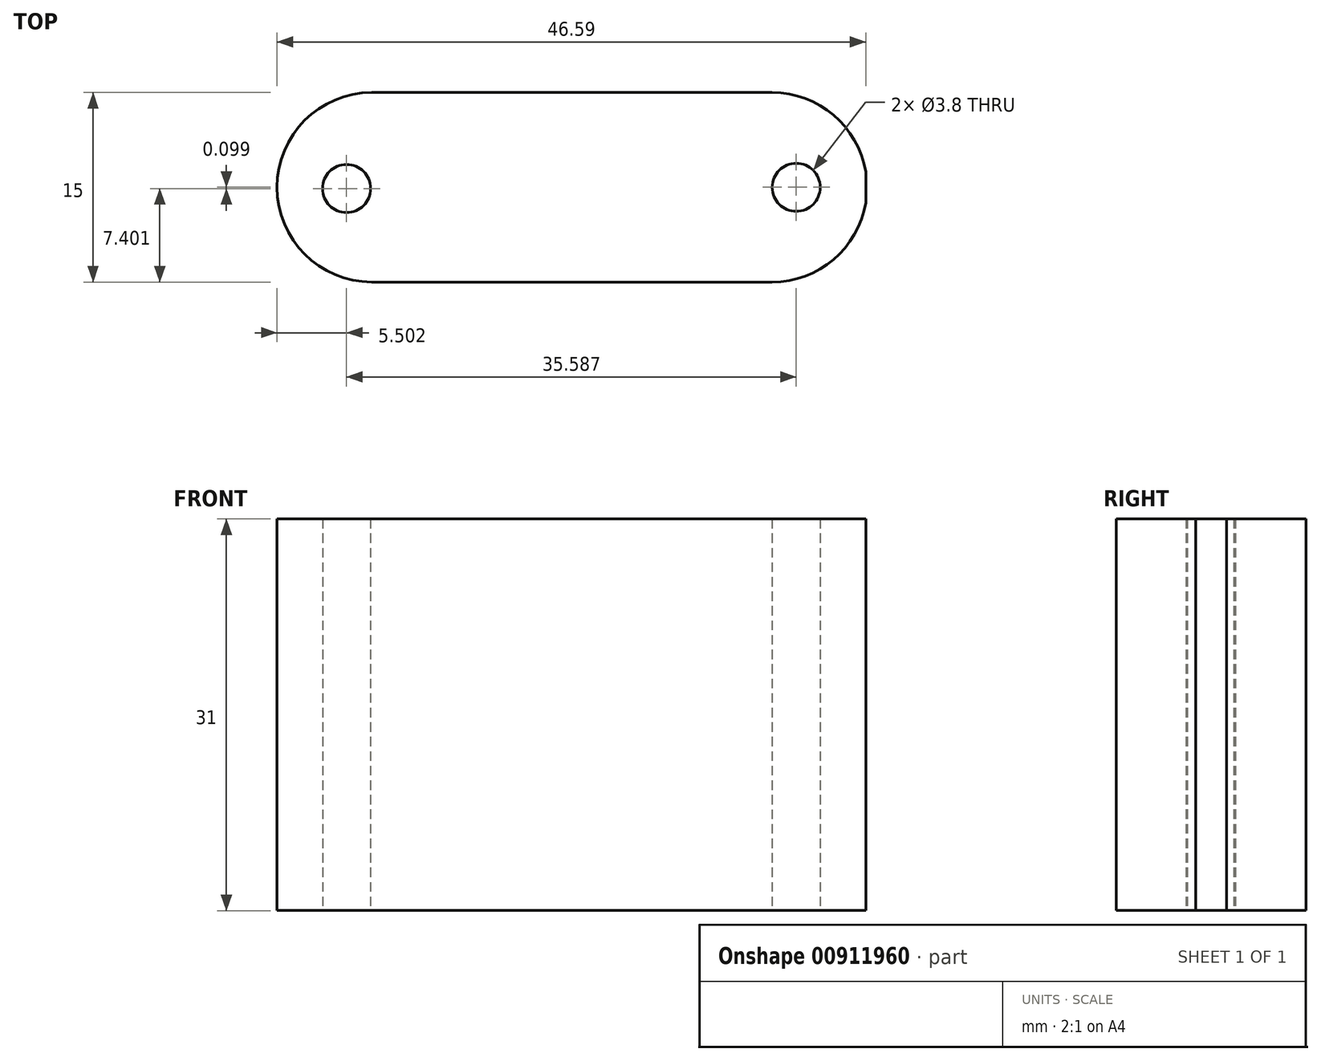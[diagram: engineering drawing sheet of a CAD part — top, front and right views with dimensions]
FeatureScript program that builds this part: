
annotation { "Feature Type Name" : "Feature", "Feature Type Description" : "" }
export const myFeature = defineFeature(function(context is Context, id is Id, definition is map)
    precondition{}
    {
        {
            var Q0;
            Q0=qCreatedBy(makeId("Front.planeOp"),FACE);
            var sketch = newSketch(context, id + "F0", { "sketchPlane" : qUnion([Q0])});
            skLineSegment(sketch, "E0.bottom", {"start": v(-92.62, 11.8) * mm, "end": v(-45.62, 11.8) * mm});
            skLineSegment(sketch, "E0.top", {"start": v(-92.62, -19.2) * mm, "end": v(-45.62, -19.2) * mm});
            skLineSegment(sketch, "E0.left", {"start": v(-92.62, 11.8) * mm, "end": v(-92.62, -19.2) * mm});
            skLineSegment(sketch, "E0.right", {"start": v(-45.62, 11.8) * mm, "end": v(-45.62, -19.2) * mm});
            skSolve(sketch);
        }
        {
            var Q0;
            Q0=qSketchRegion(id+"F0",true);
            extrude(context, id + "F1", {"entities" : qUnion([Q0]), "depth" : 15 * mm, "offsetDistance" : 25 * mm});
        }
        {
            var Q0;
            Q0=makeQuery(id+"F1.opExtrude","SWEPT_FACE",FACE,{"disambiguationData":[OSD([sQuery(id+"F0.wireOp",EDGE,"E0.top")])]});
            var sketch = newSketch(context, id + "F2", { "sketchPlane" : qUnion([Q0])});
            skCircle(sketch, "E1", {"center": v(-51.12, 7.5) * mm, "radius": 1.9 * mm});
            skSolve(sketch);
        }
        {
            var Q0;
            Q0=qSketchRegion(id+"F2",true);
            extrude(context, id + "F3", {"entities" : qUnion([Q0]), "operationType" : NewBodyOperationType.REMOVE, "oppositeDirection" : true, "depth" : 60 * mm, "offsetDistance" : 25 * mm});
        }
        {
            var Q0;
            Q0=makeQuery(id+"F1.opExtrude","SWEPT_FACE",FACE,{"disambiguationData":[OSD([sQuery(id+"F0.wireOp",EDGE,"E0.top")])]});
            var sketch = newSketch(context, id + "F4", { "sketchPlane" : qUnion([Q0])});
            skArc(sketch, "E2", {"start": v(-84.7, 15) * mm, "mid": v(-92.2, 7.5) * mm, "end": v(-84.7, 0) * mm});
            skLineSegment(sketch, "E3", {"start": v(-84.7, 0) * mm, "end": v(-92.62, 0) * mm});
            skLineSegment(sketch, "E4", {"start": v(-92.62, 0) * mm, "end": v(-92.62, 15) * mm});
            skLineSegment(sketch, "E5", {"start": v(-92.62, 15) * mm, "end": v(-84.7, 15) * mm});
            skSolve(sketch);
        }
        {
            var Q0;
            Q0=qSketchRegion(id+"F4",true);
            extrude(context, id + "F5", {"entities" : qUnion([Q0]), "operationType" : NewBodyOperationType.REMOVE, "oppositeDirection" : true, "depth" : 70 * mm, "offsetDistance" : 25 * mm});
        }
        {
            var Q0;
            Q0=makeQuery(id+"F1.opExtrude","SWEPT_FACE",FACE,{"disambiguationData":[OSD([sQuery(id+"F0.wireOp",EDGE,"E0.top")])]});
            var sketch = newSketch(context, id + "F6", { "sketchPlane" : qUnion([Q0])});
            skPoint(sketch, "E6.orphan", {"position": v(-92.2, 7.5) * mm});
            skCircle(sketch, "E7", {"center": v(-86.7, 7.6) * mm, "radius": 1.9 * mm});
            skSolve(sketch);
        }
        {
            var Q0;
            Q0=qSketchRegion(id+"F6",true);
            extrude(context, id + "F7", {"entities" : qUnion([Q0]), "operationType" : NewBodyOperationType.REMOVE, "oppositeDirection" : true, "depth" : 80 * mm, "offsetDistance" : 25 * mm});
        }
        {
            var Q0;
            Q0=makeQuery(id+"F1.opExtrude","SWEPT_FACE",FACE,{"disambiguationData":[OSD([sQuery(id+"F0.wireOp",EDGE,"E0.top")])]});
            var sketch = newSketch(context, id + "F8", { "sketchPlane" : qUnion([Q0])});
            skArc(sketch, "E8", {"start": v(19.68, 0) * mm, "mid": v(27.18, 7.5) * mm, "end": v(19.68, 15) * mm});
            skLineSegment(sketch, "E9", {"start": v(-45.62, 15) * mm, "end": v(19.68, 15) * mm});
            skLineSegment(sketch, "E10", {"start": v(-45.62, 15) * mm, "end": v(-45.62, 0) * mm});
            skLineSegment(sketch, "E11", {"start": v(19.68, 0) * mm, "end": v(-45.62, 0) * mm});
            skSolve(sketch);
        }
        {
            var Q0;
            Q0=qSketchRegion(id+"F8",true);
            extrude(context, id + "F9", {"entities" : qUnion([Q0]), "operationType" : NewBodyOperationType.REMOVE, "oppositeDirection" : true, "depth" : 70 * mm, "offsetDistance" : 25 * mm});
        }
        {
            var Q0;
            Q0=makeQuery(id+"F1.opExtrude","SWEPT_FACE",FACE,{"disambiguationData":[OSD([sQuery(id+"F0.wireOp",EDGE,"E0.bottom")])]});
            var sketch = newSketch(context, id + "F10", { "sketchPlane" : qUnion([Q0])});
            skArc(sketch, "E12", {"start": v(-53.02, -15) * mm, "mid": v(-45.52, -7.5) * mm, "end": v(-53.02, 0) * mm});
            skLineSegment(sketch, "E13", {"start": v(-53.02, 0) * mm, "end": v(-45.62, 0) * mm});
            skLineSegment(sketch, "E14", {"start": v(-45.62, 0) * mm, "end": v(-45.62, -15) * mm});
            skLineSegment(sketch, "E15", {"start": v(-45.62, -15) * mm, "end": v(-53.02, -15) * mm});
            skPoint(sketch, "E16", {"position": v(-45.62, -7.5) * mm});
            skSolve(sketch);
        }
        {
            var Q0;
            Q0 = qSketchRegion(id + "F10", true);
            extrude(context, id + "F11", {"entities" : qUnion([Q0]), "operationType" : NewBodyOperationType.REMOVE, "oppositeDirection" : true, "depth" : 70 * mm, "offsetDistance" : 25 * mm});
        }
    });
